# Revit family: BE_24861_de_DE
name_source: partatom
category: Leuchten
units: mm (PartAtom-declared; Revit-internal decimal feet)

## family parameters
Basisbauteil = Fläche
Beim Laden mit Abzugskörper schneiden = Ja
Bemaßung runder Anschluss = Durchmesser verwenden
Gemeinsam genutzt = Nein
Lichtquelle = Ja
Raumberechnungspunkt = Ja
Teiletyp = Normal

## types (4) — shared parameters
AC/DC = AC/DC
Aktualisierung = 2023-11-06T04:00:03
Befestigungsabstand = 210 mm
Befestigungsbohrung = Ø 6 mm
Beschreibung = Deckenaufbau-Tiefstrahler
Beschreibung_Sonderanfertigung = Hier können Sie Informationen zur Sonderanfertigung eintragen.
CE_Konformität = ja
Energieeffizienzklasse = LED A++ - A
Farbfilter = 16777215
Farbtemperaturverschiebung bei Dämpfen der Lampe = <Keine Auswahl>
Farbwiedergabeindex = CRI > 80
Frequenz = 0/50-60 Hz
Gewicht = 3.3 kg
Hersteller = BEGA
Lampe = LED 16.5 W
Lastklassifizierung = Beleuchtung
Lebensdauerkriterien = L80B50 @ ta 25 °C = 150000 h
Material_03 = BEGA_Oberfläche_Weiss_matt
Material_10 = BEGA_Glas_matt
Material_15 = BEGA_Leuchtmedium_matt
Material_17 = BEGA_Reflektor
Neigungswinkel = 0.00°
Produktdatenblatt = https://cdn.bega.com
Scheinlast = 0 VA
Schutzart = IP 65
Schutzklasse = I
Sonderanfertigung = Nein
Spannung = 240 V
URL = https://www.bega.com
Umgebungstemperatur = 25 °C
zero-valued in all types: Vorgabe-Ansicht

## per-type parameters (varying)
| type | Bestellnummer | Datei für fotometrisches Netz | Farbtemperatur | LED_Modulbezeichnung | Lampenlichtstrom | Leuchtenlichtstrom | M_G | M_W | Modell |
| BEGA_24861_Grafit_K4 | 24861K4 | BE_24861K4.ies | 4000 K | LED-1344/840 | 3030 lm | 2413 lm | Ja | Nein | 24861K4 |
| BEGA_24861_Weiß_K4 | 24861WK4 | BE_24861K4.ies | 4000 K | LED-1344/840 | 3030 lm | 2413 lm | Nein | Ja | 24861WK4 |
| BEGA_24861_Weiß_K3 | 24861WK3 | BE_24861K3.ies | 3000 K | LED-1344/830 | 2885 lm | 2298 lm | Nein | Ja | 24861WK3 |
| BEGA_24861_Grafit_K3 | 24861K3 | BE_24861K3.ies | 3000 K | LED-1344/830 | 2885 lm | 2298 lm | Ja | Nein | 24861K3 |
